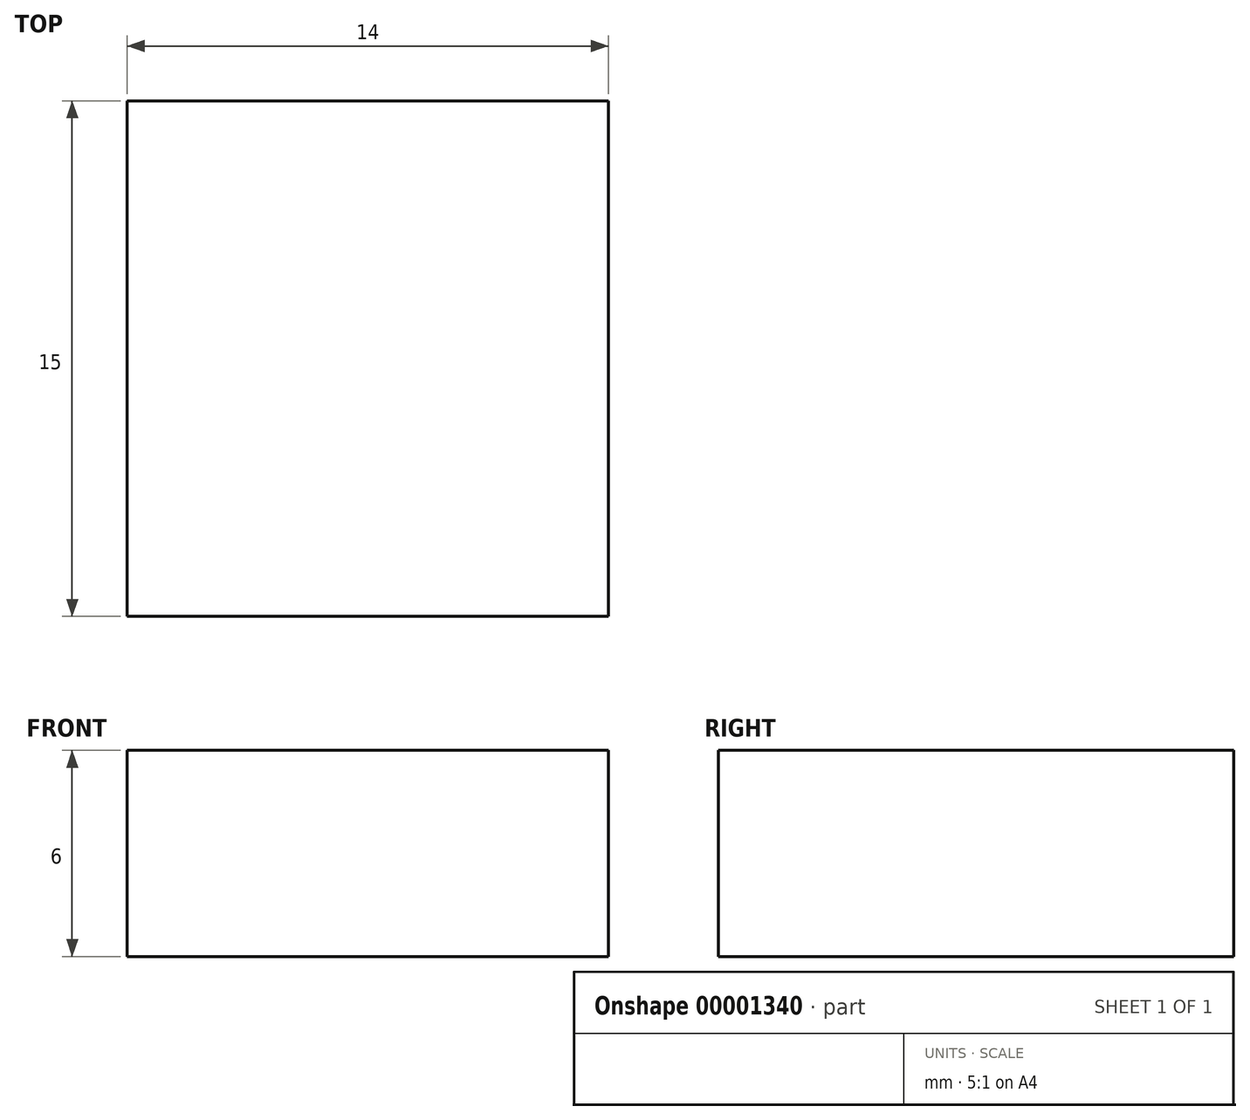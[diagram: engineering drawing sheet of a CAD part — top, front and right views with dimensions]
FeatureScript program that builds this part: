
annotation { "Feature Type Name" : "Feature", "Feature Type Description" : "" }
export const myFeature = defineFeature(function(context is Context, id is Id, definition is map)
    precondition{}
    {
        {
            var Q0;
            Q0=qCreatedBy(makeId("Front.planeOp"),FACE);
            var sketch = newSketch(context, id + "F0", { "sketchPlane" : qUnion([Q0])});
            skLineSegment(sketch, "E0.bottom", {"start": v(-14, 6) * mm, "end": v(0, 6) * mm});
            skLineSegment(sketch, "E0.top", {"start": v(-14, 0) * mm, "end": v(0, 0) * mm});
            skLineSegment(sketch, "E0.left", {"start": v(-14, 6) * mm, "end": v(-14, 0) * mm});
            skLineSegment(sketch, "E0.right", {"start": v(0, 6) * mm, "end": v(0, 0) * mm});
            skSolve(sketch);
        }
        {
            var Q0;
            Q0=makeQuery(id+"F0.imprint","IMPRINT",FACE,{"disambiguationData":[TD([[makeQuery(id+"F0.imprint","IMPRINT",EDGE,{"derivedFrom":sQuery(id+"F0.wireOp",EDGE,"E0.bottom")}),-1.0]])]});
            extrude(context, id + "F1", {"entities" : qUnion([Q0]), "depth" : 15 * mm});
        }
    });
